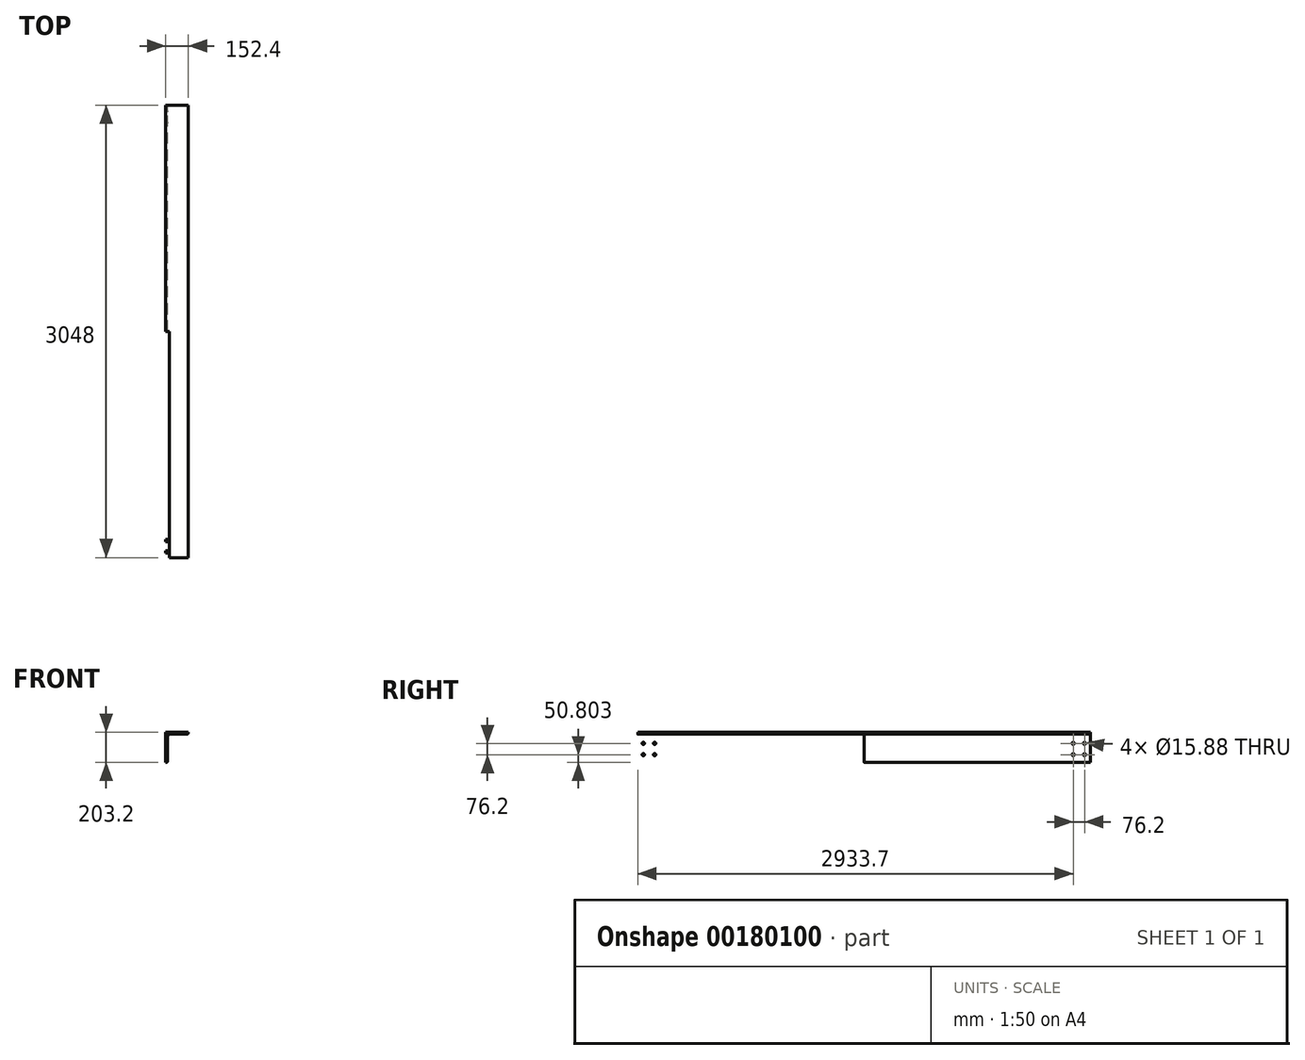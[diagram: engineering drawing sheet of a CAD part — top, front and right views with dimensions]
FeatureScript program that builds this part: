
annotation { "Feature Type Name" : "Feature", "Feature Type Description" : "" }
export const myFeature = defineFeature(function(context is Context, id is Id, definition is map)
    precondition{}
    {
        {
            var Q0;
            Q0=qCreatedBy(makeId("Front.planeOp"),FACE);
            var sketch = newSketch(context, id + "F0", { "sketchPlane" : qUnion([Q0])});
            skLineSegment(sketch, "E0.bottom", {"start": v(-67.04, 130.84) * mm, "end": v(85.36, 130.84) * mm});
            skLineSegment(sketch, "E0.top", {"start": v(-67.04, -72.36) * mm, "end": v(-63.86, -72.36) * mm});
            skLineSegment(sketch, "E0.left", {"start": v(-67.04, 130.84) * mm, "end": v(-67.04, -72.36) * mm});
            skLineSegment(sketch, "E0.right", {"start": v(85.36, 130.84) * mm, "end": v(85.36, 127.67) * mm});
            skLineSegment(sketch, "E1.0", {"start": v(-35.29, 118.14) * mm, "end": v(75.84, 118.14) * mm});
            skLineSegment(sketch, "E2.0", {"start": v(-54.34, 99.1) * mm, "end": v(-54.34, -62.83) * mm});
            skArc(sketch, "E3.filletArc", {"start": v(-35.29, 118.14) * mm, "mid": v(-48.76, 112.56) * mm, "end": v(-54.34, 99.1) * mm});
            skArc(sketch, "E4.filletArc", {"start": v(75.84, 118.14) * mm, "mid": v(82.58, 120.93) * mm, "end": v(85.36, 127.67) * mm});
            skArc(sketch, "E5.filletArc", {"start": v(-63.86, -72.36) * mm, "mid": v(-57.12, -69.57) * mm, "end": v(-54.34, -62.83) * mm});
            skSolve(sketch);
        }
        {
            var Q0;
            Q0=makeQuery(id+"F0.imprint","IMPRINT",FACE,{"disambiguationData":[TD([[makeQuery(id+"F0.imprint","IMPRINT",EDGE,{"derivedFrom":sQuery(id+"F0.wireOp",EDGE,"E0.bottom")}),-1.0]])]});
            extrude(context, id + "F1", {"entities" : qUnion([Q0]), "depth" : 3048 * mm});
        }
        {
            var Q0;
            Q0=makeQuery(id+"F1.opExtrude","SWEPT_FACE",FACE,{"disambiguationData":[OSD([sQuery(id+"F0.wireOp",EDGE,"E0.left")])]});
            var sketch = newSketch(context, id + "F2", { "sketchPlane" : qUnion([Q0])});
            skCircle(sketch, "E6", {"center": v(38.1, 54.64) * mm, "radius": 7.94 * mm});
            skCircle(sketch, "E7", {"center": v(38.1, -21.56) * mm, "radius": 7.94 * mm});
            skCircle(sketch, "E8", {"center": v(114.3, -21.56) * mm, "radius": 7.94 * mm});
            skCircle(sketch, "E9", {"center": v(114.3, 54.64) * mm, "radius": 7.94 * mm});
            skLineSegment(sketch, "E10", {"start": v(1524, 130.84) * mm, "end": v(1524, -72.36) * mm});
            skCircle(sketch, "E11.MirrorC", {"center": v(2933.7, -21.56) * mm, "radius": 7.94 * mm});
            skCircle(sketch, "E12.MirrorC", {"center": v(3009.9, -21.56) * mm, "radius": 7.94 * mm});
            skCircle(sketch, "E13.MirrorC", {"center": v(2933.7, 54.64) * mm, "radius": 7.94 * mm});
            skCircle(sketch, "E14.MirrorC", {"center": v(3009.9, 54.64) * mm, "radius": 7.94 * mm});
            skSolve(sketch);
        }
        {
            var Q0;
            Q0=makeQuery(id+"F2.imprint","IMPRINT",FACE,{"disambiguationData":[TD([[makeQuery(id+"F2.imprint","IMPRINT",EDGE,{"derivedFrom":sQuery(id+"F2.wireOp",EDGE,"E6")}),1.0]])]});
            var Q1;
            Q1=makeQuery(id+"F2.imprint","IMPRINT",FACE,{"disambiguationData":[TD([[makeQuery(id+"F2.imprint","IMPRINT",EDGE,{"derivedFrom":sQuery(id+"F2.wireOp",EDGE,"E9")}),1.0]])]});
            var Q2;
            Q2=makeQuery(id+"F2.imprint","IMPRINT",FACE,{"disambiguationData":[TD([[makeQuery(id+"F2.imprint","IMPRINT",EDGE,{"derivedFrom":sQuery(id+"F2.wireOp",EDGE,"E7")}),1.0]])]});
            var Q3;
            Q3=makeQuery(id+"F2.imprint","IMPRINT",FACE,{"disambiguationData":[TD([[makeQuery(id+"F2.imprint","IMPRINT",EDGE,{"derivedFrom":sQuery(id+"F2.wireOp",EDGE,"E8")}),1.0]])]});
            var Q4;
            Q4=makeQuery(id+"F2.imprint","IMPRINT",FACE,{"disambiguationData":[TD([[makeQuery(id+"F2.imprint","IMPRINT",EDGE,{"derivedFrom":sQuery(id+"F2.wireOp",EDGE,"E13.MirrorC")}),-1.0]])]});
            var Q5;
            Q5=makeQuery(id+"F2.imprint","IMPRINT",FACE,{"disambiguationData":[TD([[makeQuery(id+"F2.imprint","IMPRINT",EDGE,{"derivedFrom":sQuery(id+"F2.wireOp",EDGE,"E14.MirrorC")}),-1.0]])]});
            var Q6;
            Q6=makeQuery(id+"F2.imprint","IMPRINT",FACE,{"disambiguationData":[TD([[makeQuery(id+"F2.imprint","IMPRINT",EDGE,{"derivedFrom":sQuery(id+"F2.wireOp",EDGE,"E12.MirrorC")}),-1.0]])]});
            var Q7;
            Q7=makeQuery(id+"F2.imprint","IMPRINT",FACE,{"disambiguationData":[TD([[makeQuery(id+"F2.imprint","IMPRINT",EDGE,{"derivedFrom":sQuery(id+"F2.wireOp",EDGE,"E11.MirrorC")}),-1.0]])]});
            var Q8;
            Q8=sQuery(id+"F2.wireOp",EDGE,"E6");
            extrude(context, id + "F3", {"entities" : qUnion([Q0, Q1, Q2, Q3, Q4, Q5, Q6, Q7]), "operationType" : NewBodyOperationType.REMOVE, "surfaceEntities" : qUnion([Q8]), "oppositeDirection" : true, "depth" : 25.4 * mm});
        }
    });
